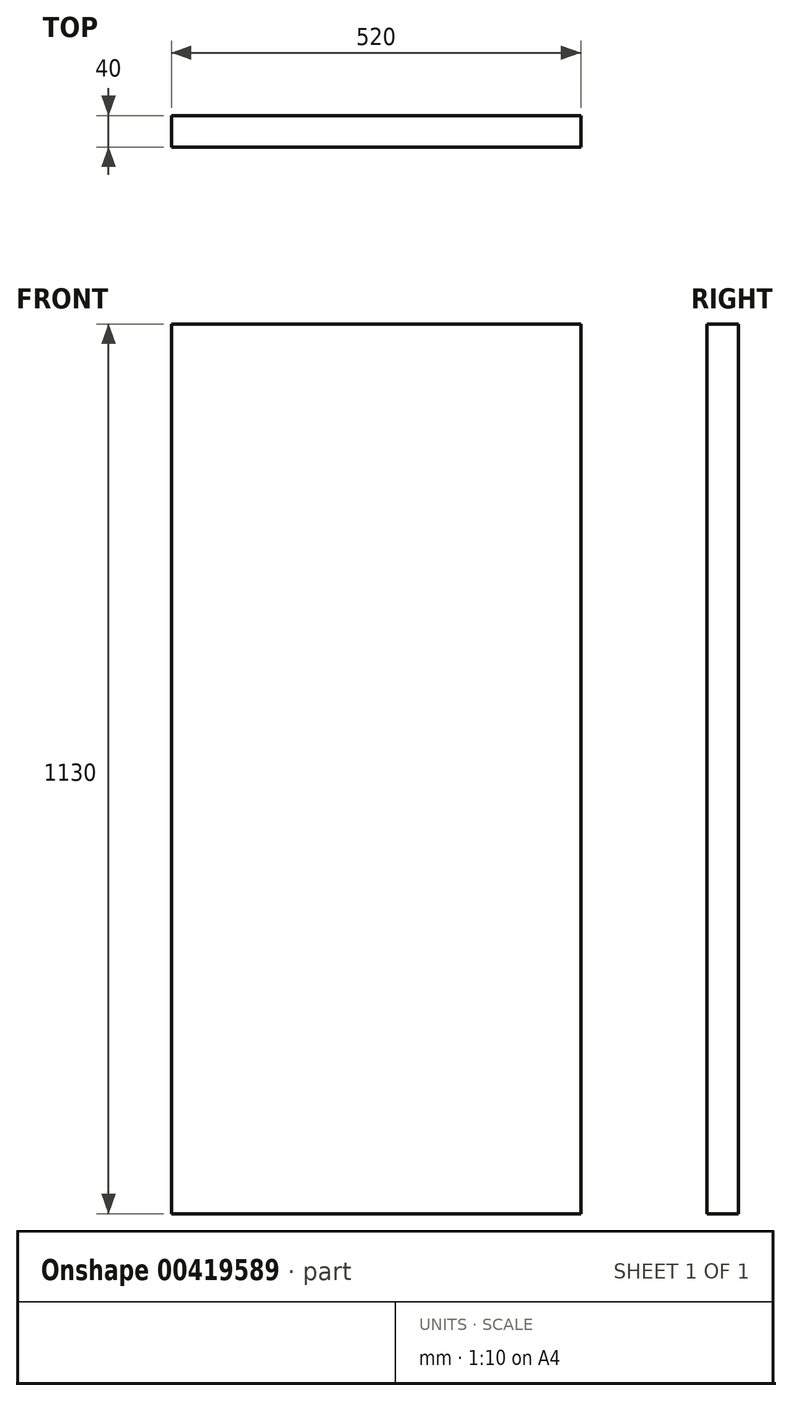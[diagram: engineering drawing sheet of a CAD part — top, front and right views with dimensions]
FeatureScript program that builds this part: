
annotation { "Feature Type Name" : "Feature", "Feature Type Description" : "" }
export const myFeature = defineFeature(function(context is Context, id is Id, definition is map)
    precondition{}
    {
        {
            var Q0;
            Q0=qCreatedBy(makeId("Top.planeOp"),FACE);
            var sketch = newSketch(context, id + "F0", { "sketchPlane" : qUnion([Q0])});
            skLineSegment(sketch, "E0.bottom", {"start": v(-411.5, 17.62) * mm, "end": v(108.5, 17.62) * mm});
            skLineSegment(sketch, "E0.top", {"start": v(-411.5, -22.38) * mm, "end": v(108.5, -22.38) * mm});
            skLineSegment(sketch, "E0.left", {"start": v(-411.5, 17.62) * mm, "end": v(-411.5, -22.38) * mm});
            skLineSegment(sketch, "E0.right", {"start": v(108.5, 17.62) * mm, "end": v(108.5, -22.38) * mm});
            skSolve(sketch);
        }
        {
            var Q0;
            Q0=makeQuery(id+"F0.imprint","IMPRINT",FACE,{"disambiguationData":[TD([[makeQuery(id+"F0.imprint","IMPRINT",EDGE,{"derivedFrom":sQuery(id+"F0.wireOp",EDGE,"E0.bottom")}),-1.0]])]});
            extrude(context, id + "F1", {"entities" : qUnion([Q0]), "depth" : 1130 * mm});
        }
    });
